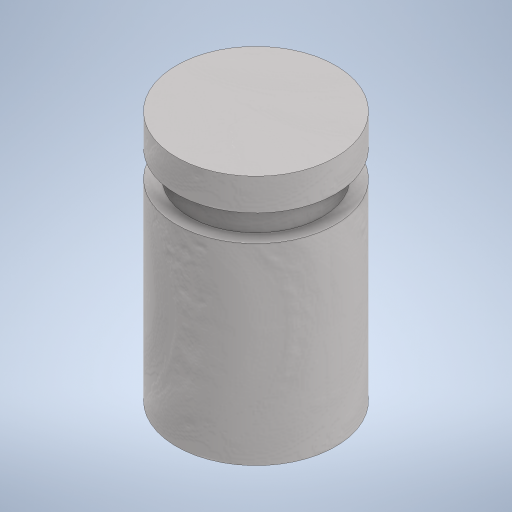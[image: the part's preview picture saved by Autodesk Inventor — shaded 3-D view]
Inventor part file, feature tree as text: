
AUTODESK INVENTOR PART (.ipt)
format: ipt  version: 2023 (Build 270158000, 158)  size: 295,424 bytes
history: native  units: mm
features: extrude x3, sketch x3, other x1
ambient origin geometry x8: Origin, YZ Plane, XZ Plane, XY Plane, X Axis, Y Axis, Z Axis, Center Point
bodies: Body1 (feature_tree)
feature tree (7):
  other  "Sólido1"
  extrude  "Extrusão1"  Depth=36.24mm TaperAngle=0.0deg
  extrude  "Extrusão2"  Depth=5.0mm TaperAngle=0.0deg
  extrude  "Extrusão3"  [1 undecoded]
  sketch  "Esboço1"  dims[d0=30.0mm d1=36.24mm d2=0.0mm]
  sketch  "Esboço2"  dims[d3=25.0mm d4=5.0mm d5=0.0mm]
  sketch  "Esboço3"  dims[d6=6.0mm d7=0.0mm]
note: 1 required parameter value undecoded (feature->parameter linkage not recoverable at this tier; creation-order binding heuristic only, values carry confidence <= 0.55)
